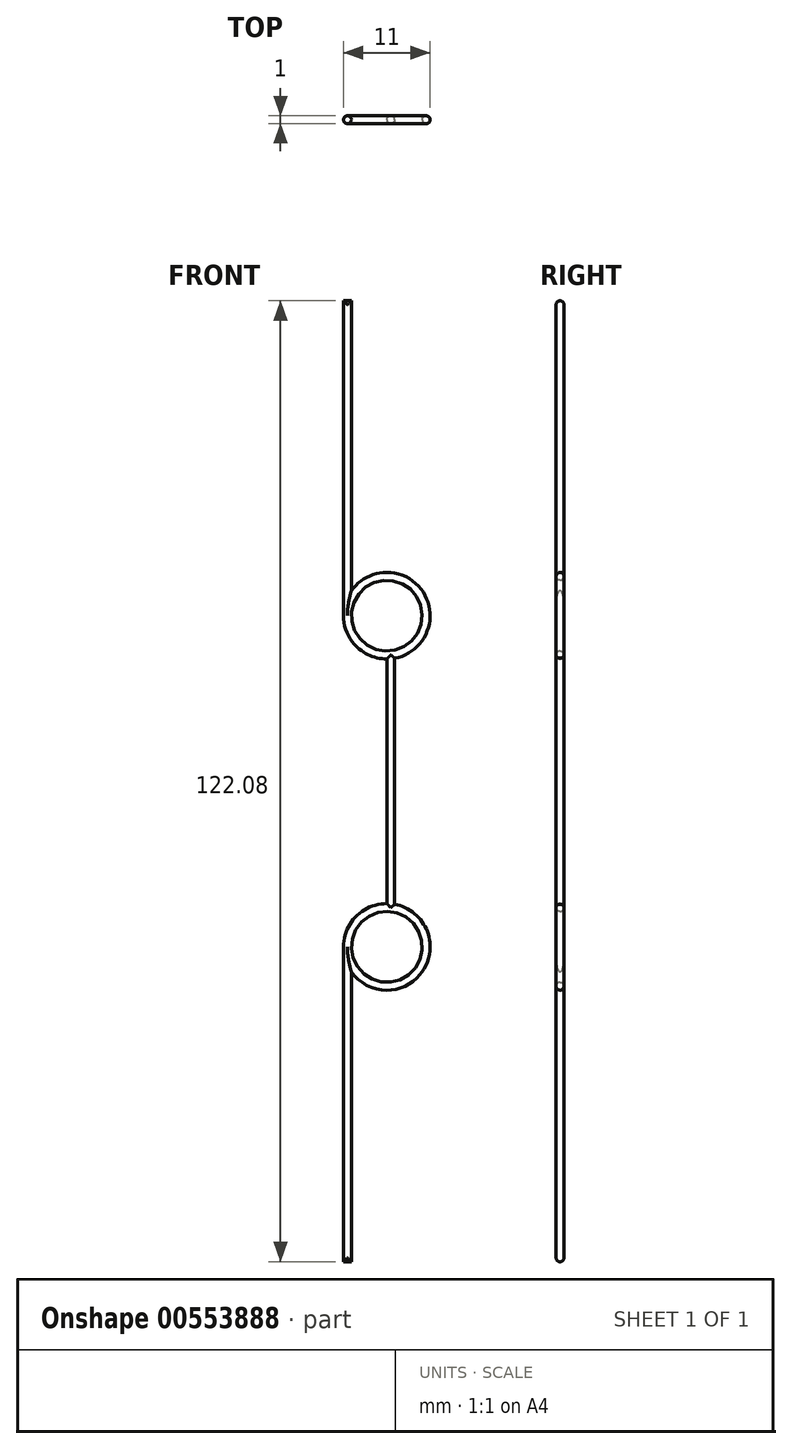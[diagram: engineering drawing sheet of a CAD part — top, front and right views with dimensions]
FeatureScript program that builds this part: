
annotation { "Feature Type Name" : "Feature", "Feature Type Description" : "" }
export const myFeature = defineFeature(function(context is Context, id is Id, definition is map)
    precondition{}
    {
        {
            var Q0;
            Q0=qCreatedBy(makeId("Front.planeOp"),FACE);
            var sketch = newSketch(context, id + "F0", { "sketchPlane" : qUnion([Q0])});
            skLineSegment(sketch, "E0", {"start": v(0, 0) * mm, "end": v(0, 40) * mm});
            skLineSegment(sketch, "E1", {"start": v(0, 40) * mm, "end": v(5.5, 40) * mm, "construction": true});
            skArc(sketch, "E2", {"start": v(1, 36.84) * mm, "mid": v(10.13, 37.03) * mm, "end": v(6.5, 45.4) * mm});
            skLineSegment(sketch, "E3", {"start": v(5.5, 45.5) * mm, "end": v(5.5, 61.04) * mm});
            skLineSegment(sketch, "E4.0", {"start": v(1, 0) * mm, "end": v(1, 36.84) * mm});
            skCircle(sketch, "E5.0", {"center": v(5.5, 40) * mm, "radius": 4.5 * mm});
            skLineSegment(sketch, "E6.0", {"start": v(6.5, 45.4) * mm, "end": v(6.5, 61.04) * mm});
            skArc(sketch, "E7.trimOffspring", {"start": v(5.5, 45.5) * mm, "mid": v(1.61, 43.89) * mm, "end": v(0, 40) * mm});
            skLineSegment(sketch, "E8", {"start": v(5.5, 61.04) * mm, "end": v(6.5, 61.04) * mm});
            skLineSegment(sketch, "E9", {"start": v(0, 0) * mm, "end": v(1, 0) * mm});
            skSolve(sketch);
        }
        {
            var Q0;
            Q0=makeQuery(id+"F0.imprint","IMPRINT",FACE,{"disambiguationData":[TD([[makeQuery(id+"F0.imprint","IMPRINT",EDGE,{"derivedFrom":sQuery(id+"F0.wireOp",EDGE,"E0")}),-1.0]])]});
            extrude(context, id + "F1", {"entities" : qUnion([Q0]), "depth" : 1 * mm, "offsetDistance" : 25 * mm});
        }
        {
            var Q0;
            Q0=makeQuery(id+"F1.opExtrude","SWEPT_BODY",BODY,{"disambiguationData":[OSD([sQuery(id+"F0.wireOp",EDGE,"E0"),sQuery(id+"F0.wireOp",EDGE,"E2"),sQuery(id+"F0.wireOp",EDGE,"E3"),sQuery(id+"F0.wireOp",EDGE,"E4.0"),sQuery(id+"F0.wireOp",EDGE,"E5.0"),sQuery(id+"F0.wireOp",EDGE,"E6.0"),sQuery(id+"F0.wireOp",EDGE,"E7.trimOffspring"),sQuery(id+"F0.wireOp",EDGE,"E8"),sQuery(id+"F0.wireOp",EDGE,"E9")])]});
            var Q1;
            Q1=makeQuery(id+"F1.opExtrude","SWEPT_FACE",FACE,{"disambiguationData":[OSD([sQuery(id+"F0.wireOp",EDGE,"E8")])]});
            mirror(context, id + "F2", {"operationType" : NewBodyOperationType.ADD, "entities" : qUnion([Q0]), "mirrorPlane" : qUnion([Q1])});
        }
        {
            var Q0;
            {var subQ0=makeQuery(id+"F1.opExtrude","CAP_FACE",FACE,{"disambiguationData":[OSD([sQuery(id+"F0.wireOp",EDGE,"E0"),sQuery(id+"F0.wireOp",EDGE,"E2"),sQuery(id+"F0.wireOp",EDGE,"E3"),sQuery(id+"F0.wireOp",EDGE,"E4.0"),sQuery(id+"F0.wireOp",EDGE,"E5.0"),sQuery(id+"F0.wireOp",EDGE,"E6.0"),sQuery(id+"F0.wireOp",EDGE,"E7.trimOffspring"),sQuery(id+"F0.wireOp",EDGE,"E8"),sQuery(id+"F0.wireOp",EDGE,"E9")])],"isStart":false});Q0=makeQuery(id+"F2.boolean.opBoolean","MERGE",FACE,{"derivedFrom":[subQ0,makeQuery(id+"F2.opPattern","COPY",FACE,{"derivedFrom":subQ0,"instanceName":"1"})]});}
            var Q1;
            {var subQ0=makeQuery(id+"F1.opExtrude","CAP_FACE",FACE,{"disambiguationData":[OSD([sQuery(id+"F0.wireOp",EDGE,"E0"),sQuery(id+"F0.wireOp",EDGE,"E2"),sQuery(id+"F0.wireOp",EDGE,"E3"),sQuery(id+"F0.wireOp",EDGE,"E4.0"),sQuery(id+"F0.wireOp",EDGE,"E5.0"),sQuery(id+"F0.wireOp",EDGE,"E6.0"),sQuery(id+"F0.wireOp",EDGE,"E7.trimOffspring"),sQuery(id+"F0.wireOp",EDGE,"E8"),sQuery(id+"F0.wireOp",EDGE,"E9")])],"isStart":true});Q1=makeQuery(id+"F2.boolean.opBoolean","MERGE",FACE,{"derivedFrom":[subQ0,makeQuery(id+"F2.opPattern","COPY",FACE,{"derivedFrom":subQ0,"instanceName":"1"})]});}
            fillet(context, id + "F3", {"entities" : qUnion([Q0, Q1]), "radius" : 0.5 * mm, "tangentPropagation" : true, "allowEdgeOverflow" : false});
        }
    });
